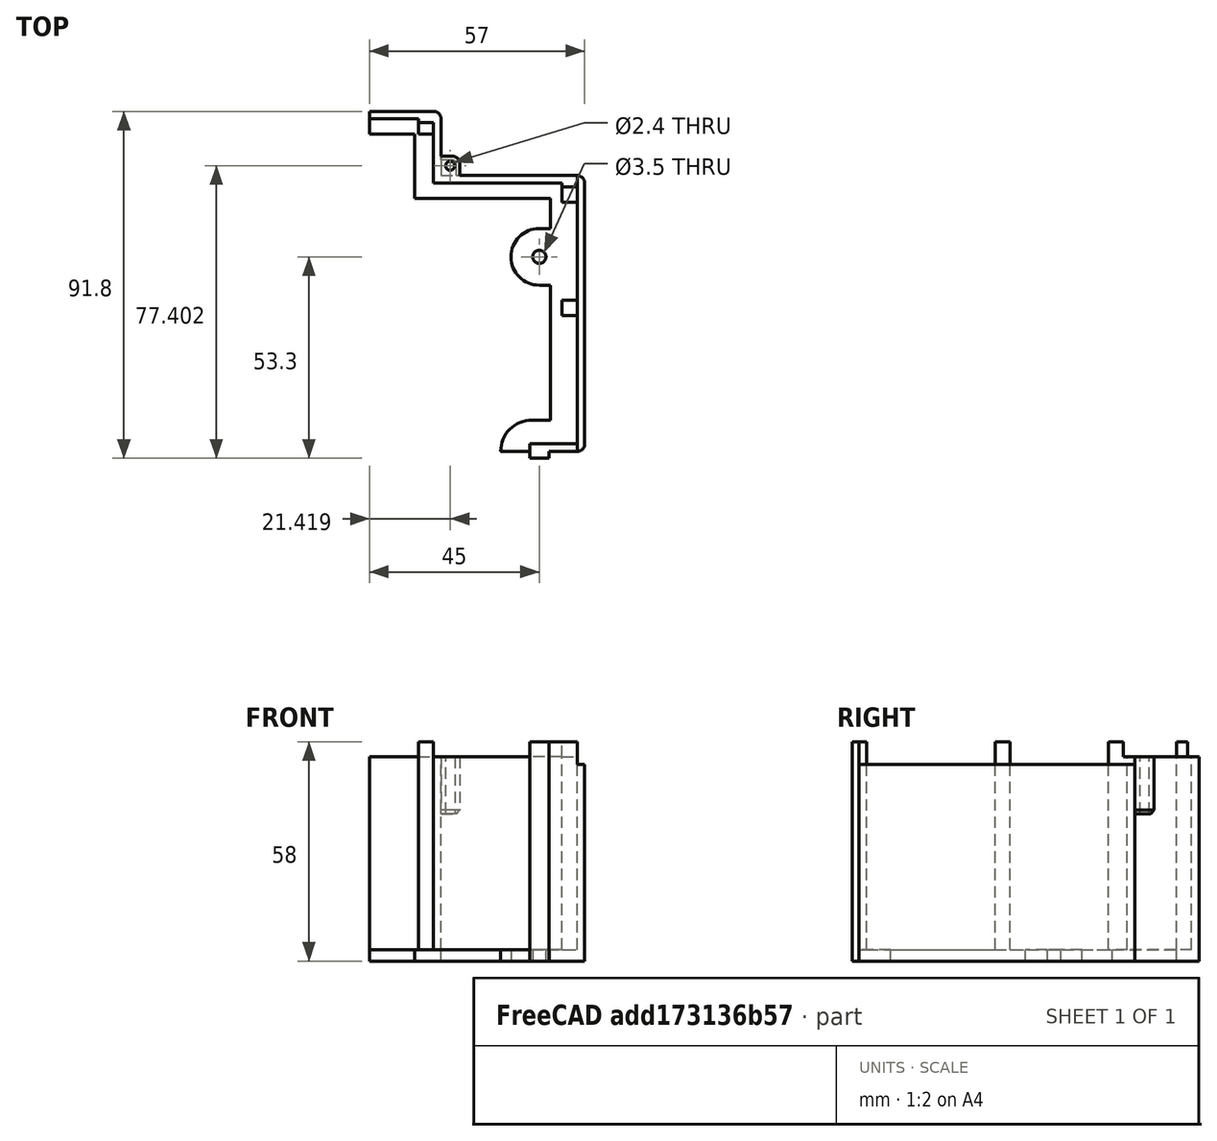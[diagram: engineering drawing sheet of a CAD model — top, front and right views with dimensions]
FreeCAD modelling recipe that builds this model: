
FCSTD DOCUMENT  (FreeCAD 0.18R)
Label: K-MINI-Enclosure-SideCoverFront
License: CreativeCommons Attribution
LicenseURL: http://creativecommons.org/licenses/by/4.0/
objects: Sketcher::SketchObject×5, PartDesign::Pad×3, PartDesign::Pocket×2, PartDesign::Chamfer×1, PartDesign::Body×1, App::Part×1, Mesh::Feature×1
note: 17 computed .brp shape members not serialized (recipe doc carries the construction recipe); baked Part::Feature solids carry a one-line shape summary decoded from their .brp

FEATURE [Sketcher::SketchObject] Sketch  label="BaseProfile"
  AttachmentOffset = pos=(0,0,3) rot=(0,0,1;0rad)
  MapMode = 5
  Placement = pos=(0,0,3) rot=(0,0,1;0rad)
  Support = -> [XY_Plane]
  sketch-geometry (24):
    g0: LineSegment StartX=-36 StartY=18 StartZ=0 EndX=0 EndY=18 EndZ=0
    g1: LineSegment StartX=2 StartY=16 StartZ=0 EndX=2 EndY=-53 EndZ=0
    g2: LineSegment StartX=-7 StartY=-46.67 StartZ=0 EndX=-7 EndY=-11 EndZ=0
    g3: LineSegment StartX=-7 StartY=-11 StartZ=0 EndX=-10 EndY=-11 EndZ=0
    g4: LineSegment StartX=-10 StartY=4 StartZ=0 EndX=-7 EndY=4 EndZ=0
    g5: LineSegment StartX=-7 StartY=4 StartZ=0 EndX=-7 EndY=12 EndZ=0
    g6: LineSegment StartX=-7 StartY=12 StartZ=0 EndX=-43 EndY=12 EndZ=0
    g7: LineSegment StartX=-43 StartY=12 StartZ=0 EndX=-43 EndY=29 EndZ=0
    g8: ArcOfCircle CenterX=-1e-16 CenterY=16 CenterZ=0 NormalX=0 NormalY=0 NormalZ=1 AngleXU=0 Radius=2 StartAngle=0 EndAngle=1.5708
    g9: ArcOfCircle CenterX=-1e-16 CenterY=-53 CenterZ=0 NormalX=0 NormalY=0 NormalZ=1 AngleXU=0 Radius=2 StartAngle=4.71239 EndAngle=6.28319
    g10: LineSegment StartX=2e-16 StartY=-55 StartZ=0 EndX=-7.5 EndY=-55 EndZ=0
    g11: Circle CenterX=-10 CenterY=-3.5 CenterZ=0 NormalX=0 NormalY=0 NormalZ=1 AngleXU=0 Radius=1.75
    g12: ArcOfCircle CenterX=-10 CenterY=-3.5 CenterZ=0 NormalX=0 NormalY=0 NormalZ=1 AngleXU=0 Radius=7.5 StartAngle=1.5708 EndAngle=4.71239
    g13: ArcOfCircle CenterX=-11.9007 CenterY=-55 CenterZ=0 NormalX=0 NormalY=0 NormalZ=1 AngleXU=0 Radius=8.33 StartAngle=1.5708 EndAngle=3.14159
    g14: LineSegment StartX=-11.9007 StartY=-46.67 StartZ=0 EndX=-7 EndY=-46.67 EndZ=0
    g15: LineSegment StartX=-55 StartY=35 StartZ=0 EndX=-38 EndY=35 EndZ=0
    g16: LineSegment StartX=-36 StartY=33 StartZ=0 EndX=-36 EndY=18 EndZ=0
    g17: LineSegment StartX=-55 StartY=35 StartZ=0 EndX=-55 EndY=29 EndZ=0
    g18: LineSegment StartX=-55 StartY=29 StartZ=0 EndX=-43 EndY=29 EndZ=0
    g19: ArcOfCircle CenterX=-38 CenterY=33 CenterZ=0 NormalX=0 NormalY=0 NormalZ=1 AngleXU=0 Radius=2 StartAngle=-1.8e-15 EndAngle=1.5708
    g20: LineSegment StartX=-20.2307 StartY=-55 StartZ=0 EndX=-12.5 EndY=-55 EndZ=0
    g21: LineSegment StartX=-12.5 StartY=-55 StartZ=0 EndX=-12.5 EndY=-56.8 EndZ=0
    g22: LineSegment StartX=-12.5 StartY=-56.8 StartZ=0 EndX=-7.5 EndY=-56.8 EndZ=0
    g23: LineSegment StartX=-7.5 StartY=-56.8 StartZ=0 EndX=-7.5 EndY=-55 EndZ=0
  constraints (65):
    c: Coincident(g2,g3)
    c: Coincident(g4,g5)
    c: Coincident(g6,g7)
    c: Horizontal(g4)
    c: Vertical(g5)
    c: Horizontal(g0)
    c: Horizontal(g6)
    c: Vertical(g7)
    c: Vertical(g1)
    c: Tangent(g0,g8) = 1.5708
    c: Tangent(g1,g8) = 1.5708
    c: Radius(g8) = 2
    c: DistanceY(g-1,g0) = 18
    c: DistanceX(g-1,g1) = 2
    c: Tangent(g1,g9) = 1.5708
    c: Horizontal(g10)
    c: Tangent(g9,g10) = 1.5708
    c: Vertical(g2)
    c: Horizontal(g3)
    c: Equal(g9,g8)
    c: DistanceY(g9,g-1) = 55
    c: Coincident(g6,g5)
    c: DistanceY(g3,g4) = 15
    c: Vertical(g2,g4)
    c: DistanceY(g5,g5) = 8
    c: Radius(g11) = 1.75
    c: DistanceX(g11,g-1) = 10
    c: Tangent(g4,g12) = 1.5708
    c: Tangent(g12,g3) = 1.5708
    c: Coincident(g11,g12)
    c: Horizontal(g14)
    c: Coincident(g14,g2)
    c: Tangent(g13,g14) = 1.5708
    c: DistanceX(g4,g-1) = 7
    c: Radius(g13) = 8.33
    c: Vertical(g16)
    c: Horizontal(g15)
    c: DistanceX(g15,g-1) = 55
    c: Coincident(g0,g16)
    c: DistanceY(g6,g0) = 6
    c: Coincident(g17,g18)
    c: Coincident(g7,g18)
    c: Horizontal(g18)
    c: Vertical(g17)
    c: Coincident(g15,g17)
    c: Radius(g19) = 2
    c: Tangent(g15,g19) = 1.5708
    c: Tangent(g16,g19) = 1.5708
    c: DistanceY(g17,g17) = 6
    c: DistanceY(g-1,g15) = 35
    c: DistanceX(g0,g-1) = 36
    c: DistanceX(g6,g0) = 7
    c: Coincident(g20,g21)
    c: Coincident(g21,g22)
    c: Coincident(g22,g23)
    c: Coincident(g10,g23)
    c: Horizontal(g22)
    c: Horizontal(g20)
    c: Vertical(g21)
    c: Vertical(g23)
    c: DistanceX(g22,g22) = 5
    c: Perpendicular(g13,g20) = 1.5708
    c: DistanceX(g22,g9) = 7.5
    c: DistanceY(g21,g21) = 1.8
    c: Horizontal(g20,g10)
FEATURE [PartDesign::Pad] Pad  label="Base"
  Length = 3
  Length2 = 100
  Profile = -> Sketch
  Type = 0
FEATURE [Sketcher::SketchObject] Sketch001  label="WallProfile"
  MapMode = 5
  Placement = pos=(0,0,6) rot=(0,0,1;0rad)
  Support = -> [Pad]
  sketch-geometry (25):
    g0: LineSegment StartX=-4 StartY=16 StartZ=0 EndX=-38 EndY=16 EndZ=0
    g1: LineSegment StartX=-36 StartY=18 StartZ=0 EndX=0 EndY=18 EndZ=0
    g2: ArcOfCircle CenterX=-1e-16 CenterY=16 CenterZ=0 NormalX=0 NormalY=0 NormalZ=1 AngleXU=0 Radius=2 StartAngle=9e-16 EndAngle=1.5708
    g3: LineSegment StartX=2 StartY=16 StartZ=0 EndX=2 EndY=-53 EndZ=0
    g4: ArcOfCircle CenterX=0 CenterY=-53 CenterZ=0 NormalX=0 NormalY=0 NormalZ=1 AngleXU=0 Radius=2 StartAngle=4.71239 EndAngle=6.28319
    g5: LineSegment StartX=2e-16 StartY=-55 StartZ=0 EndX=-7.5 EndY=-55 EndZ=0
    g6: LineSegment StartX=-12.5 StartY=-53 StartZ=0 EndX=0 EndY=-53 EndZ=0
    g7: LineSegment StartX=0 StartY=-15 StartZ=0 EndX=0 EndY=11 EndZ=0
    g8: LineSegment StartX=-55 StartY=35 StartZ=0 EndX=-55 EndY=33 EndZ=0
    g9: LineSegment StartX=-4 StartY=16 StartZ=0 EndX=-4 EndY=11 EndZ=0
    g10: LineSegment StartX=-4 StartY=11 StartZ=0 EndX=0 EndY=11 EndZ=0
    g11: LineSegment StartX=0 StartY=-53 StartZ=0 EndX=0 EndY=-19 EndZ=0
    g12: LineSegment StartX=0 StartY=-19 StartZ=0 EndX=-4 EndY=-19 EndZ=0
    g13: LineSegment StartX=-4 StartY=-19 StartZ=0 EndX=-4 EndY=-15 EndZ=0
    g14: LineSegment StartX=-4 StartY=-15 StartZ=0 EndX=0 EndY=-15 EndZ=0
    g15: LineSegment StartX=-55 StartY=33 StartZ=0 EndX=-42 EndY=33 EndZ=0
    g16: LineSegment StartX=-42 StartY=33 StartZ=0 EndX=-42 EndY=29 EndZ=0
    g17: LineSegment StartX=-55 StartY=35 StartZ=0 EndX=-38 EndY=35 EndZ=0
    g18: ArcOfCircle CenterX=-38 CenterY=33 CenterZ=0 NormalX=0 NormalY=0 NormalZ=1 AngleXU=0 Radius=2 StartAngle=1.4e-15 EndAngle=1.5708
    g19: LineSegment StartX=-36 StartY=33 StartZ=0 EndX=-36 EndY=18 EndZ=0
    g20: LineSegment StartX=-7.5 StartY=-55 StartZ=0 EndX=-7.5 EndY=-56.8 EndZ=0
    g21: LineSegment StartX=-7.5 StartY=-56.8 StartZ=0 EndX=-12.5 EndY=-56.8 EndZ=0
    g22: LineSegment StartX=-12.5 StartY=-56.8 StartZ=0 EndX=-12.5 EndY=-53 EndZ=0
    g23: LineSegment StartX=-42 StartY=29 StartZ=0 EndX=-38 EndY=29 EndZ=0
    g24: LineSegment StartX=-38 StartY=29 StartZ=0 EndX=-38 EndY=16 EndZ=0
  constraints (72):
    c: Tangent(g1,g2) = 1.5708
    c: Tangent(g2,g3) = 1.5708
    c: Tangent(g3,g4) = 1.5708
    c: Tangent(g4,g5) = 1.5708
    c: Vertical(g7)
    c: Vertical(g3)
    c: Horizontal(g1)
    c: Radius(g2) = 2
    c: Equal(g4,g2)
    c: Horizontal(g5)
    c: Horizontal(g6)
    c: Vertical(g8)
    c: DistanceY(g-1,g1) = 18
    c: Horizontal(g0)
    c: DistanceX(g-1,g2) = 2
    c: DistanceY(g5,g-1) = 55
    c: Coincident(g9,g10)
    c: Coincident(g11,g12)
    c: Coincident(g12,g13)
    c: Coincident(g13,g14)
    c: Coincident(g7,g14)
    c: Horizontal(g14)
    c: Horizontal(g12)
    c: Vertical(g9)
    c: Coincident(g0,g9)
    c: Coincident(g7,g10)
    c: Horizontal(g10)
    c: Vertical(g11)
    c: Coincident(g6,g11)
    c: Vertical(g13)
    c: Vertical(g7,g11)
    c: Vertical(g9,g13)
    c: DistanceX(g6,g3) = 2
    c: DistanceX(g8,g-1) = 55
    c: Tangent(g17,g18) = 1.5708
    c: Tangent(g18,g19) = 1.5708
    c: Vertical(g19)
    c: Vertical(g16)
    c: Horizontal(g15)
    c: Horizontal(g17)
    c: Coincident(g1,g19)
    c: Coincident(g8,g17)
    c: Radius(g18) = 2
    c: DistanceY(g-1,g17) = 35
    c: DistanceY(g13,g13) = 4
    c: Coincident(g20,g21)
    c: Coincident(g21,g22)
    c: Vertical(g22)
    c: Horizontal(g21)
    c: Coincident(g5,g20)
    c: Vertical(g20)
    c: DistanceX(g5,g4) = 7.5
    c: DistanceX(g21,g21) = 5
    c: DistanceY(g20,g20) = 1.8
    c: Coincident(g22,g6)
    c: DistanceY(g4,g6) = 2
    c: DistanceX(g12,g12) = 4
    c: DistanceY(g7,g-1) = 15
    c: Coincident(g23,g24)
    c: Horizontal(g23)
    c: Vertical(g24)
    c: Coincident(g24,g0)
    c: Coincident(g23,g16)
    c: DistanceY(g0,g1) = 2
    c: Coincident(g15,g8)
    c: DistanceX(g18,g2) = 38
    c: Coincident(g15,g16)
    c: DistanceX(g23,g23) = 4
    c: DistanceY(g16,g16) = 4
    c: DistanceY(g9,g9) = 5
    c: DistanceY(g8,g8) = 2
    c: DistanceX(g0,g1) = 2
FEATURE [PartDesign::Pad] Pad001  label="Wall"
  BaseFeature = -> Pad
  Length = 55
  Length2 = 100
  Profile = -> Sketch001
  Type = 0
FEATURE [Sketcher::SketchObject] Sketch002  label="Polycarbonate-Side-Cover-Profile"
  MapMode = 5
  Placement = pos=(0,0,61) rot=(0,0,1;0rad)
  Support = -> [Pad001]
  sketch-geometry (4):
    g0: LineSegment StartX=0 StartY=93.0926 StartZ=0 EndX=2 EndY=93.0926 EndZ=0
    g1: LineSegment StartX=2 StartY=93.0926 StartZ=0 EndX=2 EndY=-66.0782 EndZ=0
    g2: LineSegment StartX=2 StartY=-66.0782 StartZ=0 EndX=0 EndY=-66.0782 EndZ=0
    g3: LineSegment StartX=0 StartY=-66.0782 StartZ=0 EndX=0 EndY=93.0926 EndZ=0
  constraints (10):
    c: Coincident(g0,g1)
    c: Coincident(g1,g2)
    c: Coincident(g2,g3)
    c: Coincident(g3,g0)
    c: Horizontal(g0)
    c: Horizontal(g2)
    c: Vertical(g1)
    c: Vertical(g3)
    c: DistanceX(g2,g2) = 2
    c: PointOnObject(g2,g-2)
FEATURE [PartDesign::Pocket] Pocket
  BaseFeature = -> Pad001
  Length = 6
  Length2 = 100
  Profile = -> Sketch002
  Type = 0
FEATURE [Sketcher::SketchObject] Sketch003  label="CoroProfile"
  AttachmentOffset = pos=(0,0,57) rot=(0,0,1;0rad)
  MapMode = 5
  Placement = pos=(0,0,57) rot=(0,0,1;0rad)
  Support = -> [XY_Plane]
  sketch-geometry (6):
    g0: LineSegment StartX=-60 StartY=115 StartZ=0 EndX=-60 EndY=32 EndZ=0
    g1: LineSegment StartX=-60 StartY=32 StartZ=0 EndX=-38 EndY=32 EndZ=0
    g2: LineSegment StartX=-38 StartY=32 StartZ=0 EndX=-38 EndY=15 EndZ=0
    g3: LineSegment StartX=-38 StartY=15 StartZ=0 EndX=0 EndY=15 EndZ=0
    g4: LineSegment StartX=0 StartY=15 StartZ=0 EndX=0 EndY=115 EndZ=0
    g5: LineSegment StartX=0 StartY=115 StartZ=0 EndX=-60 EndY=115 EndZ=0
  constraints (18):
    c: Coincident(g0,g1)
    c: Coincident(g1,g2)
    c: Coincident(g2,g3)
    c: Coincident(g3,g4)
    c: Coincident(g4,g5)
    c: Vertical(g4)
    c: Vertical(g0)
    c: Vertical(g2)
    c: Horizontal(g1)
    c: Horizontal(g5)
    c: Horizontal(g3)
    c: Coincident(g0,g5)
    c: PointOnObject(g3,g-2)
    c: DistanceX(g3,g3) = 38
    c: DistanceY(g2,g2) = 17
    c: DistanceY(g-1,g3) = 15
    c: DistanceX(g5,g5) = 60
    c: DistanceY(g4,g4) = 100
FEATURE [PartDesign::Pocket] Pocket001  label="CoroSheet"
  BaseFeature = -> Pocket
  Length = 5
  Length2 = 100
  Profile = -> Sketch003
  Reversed = true
  Type = 0
FEATURE [Sketcher::SketchObject] Sketch004
  MapMode = 5
  Placement = pos=(0,0,57) rot=(0,0,1;0rad)
  Support = -> [Pocket001]
  sketch-geometry (6):
    g0: ArcOfCircle CenterX=-33.0033 CenterY=21.1214 CenterZ=0 NormalX=0 NormalY=0 NormalZ=1 AngleXU=0 Radius=2 StartAngle=8e-16 EndAngle=1.5708
    g1: LineSegment StartX=-33.0033 StartY=23.1214 StartZ=0 EndX=-36 EndY=23.1214 EndZ=0
    g2: LineSegment StartX=-36 StartY=23.1214 StartZ=0 EndX=-36 EndY=17.7848 EndZ=0
    g3: LineSegment StartX=-36 StartY=17.7848 StartZ=0 EndX=-31.0033 EndY=17.7848 EndZ=0
    g4: LineSegment StartX=-31.0033 StartY=17.7848 StartZ=0 EndX=-31.0033 EndY=21.1214 EndZ=0
    g5: Circle CenterX=-33.5811 CenterY=20.6024 CenterZ=0 NormalX=0 NormalY=0 NormalZ=1 AngleXU=0 Radius=1.2
  constraints (12):
    c: Coincident(g1,g2)
    c: Coincident(g2,g3)
    c: Coincident(g3,g4)
    c: Tangent(g0,g1) = -1.5708
    c: Tangent(g0,g4) = -1.5708
    c: Vertical(g4)
    c: Horizontal(g3)
    c: Vertical(g2)
    c: Horizontal(g1)
    c: Radius(g0) = 2
    c: Radius(g5) = 1.2
    c: DistanceX(g2,g-1) = 36
FEATURE [PartDesign::Pad] Pad002
  BaseFeature = -> Pocket001
  Length = 15
  Length2 = 100
  Profile = -> Sketch004
  Reversed = true
  Type = 0
FEATURE [PartDesign::Chamfer] Chamfer
  Base = -> Pad002 [Edge87]
  BaseFeature = -> Pad002
  Size = 1
FEATURE [PartDesign::Body] Body  label="SideCoverFront"
  Group = -> [Sketch,Pad,Sketch001,Pad001,Sketch002,Pocket,Sketch003,Pocket001,Sketch004,Pad002,Chamfer]
  Origin = -> Origin
  Tip = -> Chamfer
FEATURE [App::Part] Part
  Group = -> [Body]
  Origin = -> Origin001
FEATURE [Mesh::Feature] Mesh  label="SideCoverFront (Meshed)"
